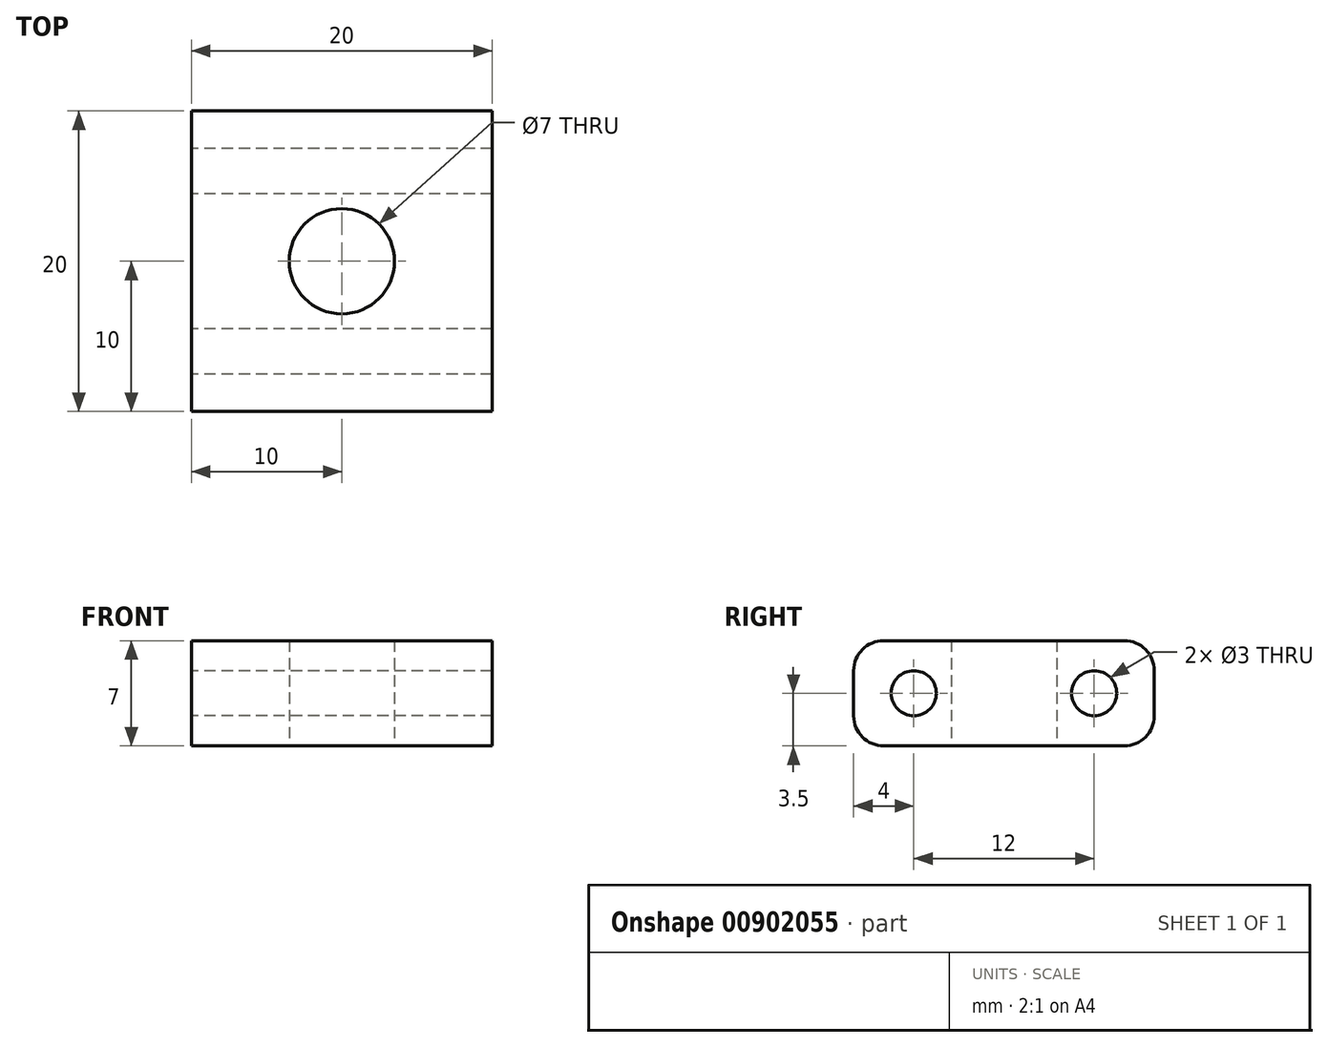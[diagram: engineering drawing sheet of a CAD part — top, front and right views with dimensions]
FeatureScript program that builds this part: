
annotation { "Feature Type Name" : "Feature", "Feature Type Description" : "" }
export const myFeature = defineFeature(function(context is Context, id is Id, definition is map)
    precondition{}
    {
        {
            var Q0;
            Q0=qCreatedBy(makeId("Top.planeOp"),FACE);
            var sketch = newSketch(context, id + "F0", { "sketchPlane" : qUnion([Q0])});
            skLineSegment(sketch, "E0.bottom", {"start": v(10, 10) * mm, "end": v(-10, 10) * mm});
            skLineSegment(sketch, "E0.top", {"start": v(10, -10) * mm, "end": v(-10, -10) * mm});
            skLineSegment(sketch, "E0.left", {"start": v(10, 10) * mm, "end": v(10, -10) * mm});
            skLineSegment(sketch, "E0.right", {"start": v(-10, 10) * mm, "end": v(-10, -10) * mm});
            skPoint(sketch, "E0.middle", {"position": v(0, 0) * mm});
            skCircle(sketch, "E1", {"center": v(0, 0) * mm, "radius": 3.5 * mm});
            skSolve(sketch);
        }
        {
            var Q0;
            Q0=makeQuery(id+"F0.imprint","IMPRINT",FACE,{"disambiguationData":[TD([[makeQuery(id+"F0.imprint","IMPRINT",EDGE,{"derivedFrom":sQuery(id+"F0.wireOp",EDGE,"E0.bottom")}),1.0]])]});
            extrude(context, id + "F1", {"entities" : qUnion([Q0]), "depth" : 7 * mm, "offsetDistance" : 25 * mm});
        }
        {
            var Q0;
            Q0=makeQuery(id+"F1.opExtrude","CAP_EDGE",EDGE,{"disambiguationData":[OSD([sQuery(id+"F0.wireOp",EDGE,"E0.top")])],"isStart":false});
            var Q1;
            Q1=makeQuery(id+"F1.opExtrude","CAP_EDGE",EDGE,{"disambiguationData":[OSD([sQuery(id+"F0.wireOp",EDGE,"E0.top")])],"isStart":true});
            var Q2;
            Q2=makeQuery(id+"F1.opExtrude","CAP_EDGE",EDGE,{"disambiguationData":[OSD([sQuery(id+"F0.wireOp",EDGE,"E0.bottom")])],"isStart":false});
            var Q3;
            Q3=makeQuery(id+"F1.opExtrude","CAP_EDGE",EDGE,{"disambiguationData":[OSD([sQuery(id+"F0.wireOp",EDGE,"E0.bottom")])],"isStart":true});
            fillet(context, id + "F2", {"entities" : qUnion([Q0, Q1, Q2, Q3]), "radius" : 2 * mm, "tangentPropagation" : true, "allowEdgeOverflow" : false});
        }
        {
            var Q0;
            Q0=makeQuery(id+"F1.opExtrude","SWEPT_FACE",FACE,{"disambiguationData":[OSD([sQuery(id+"F0.wireOp",EDGE,"E0.right")])]});
            var sketch = newSketch(context, id + "F3", { "sketchPlane" : qUnion([Q0])});
            skLineSegment(sketch, "E2", {"start": v(-10, 3.5) * mm, "end": v(-6, 3.5) * mm, "construction": true});
            skLineSegment(sketch, "E3", {"start": v(-6, 3.5) * mm, "end": v(-6, 7) * mm, "construction": true});
            skLineSegment(sketch, "E4", {"start": v(10, 3.5) * mm, "end": v(6, 3.5) * mm, "construction": true});
            skLineSegment(sketch, "E5", {"start": v(6, 3.5) * mm, "end": v(6, 7) * mm, "construction": true});
            skCircle(sketch, "E6", {"center": v(-6, 3.5) * mm, "radius": 1.5 * mm});
            skCircle(sketch, "E7", {"center": v(6, 3.5) * mm, "radius": 1.5 * mm});
            skSolve(sketch);
        }
        {
            var Q0;
            Q0 = qSketchRegion(id + "F3", true);
            extrude(context, id + "F4", {"entities" : qUnion([Q0]), "operationType" : NewBodyOperationType.REMOVE, "oppositeDirection" : true, "depth" : 25 * mm, "offsetDistance" : 25 * mm});
        }
    });
